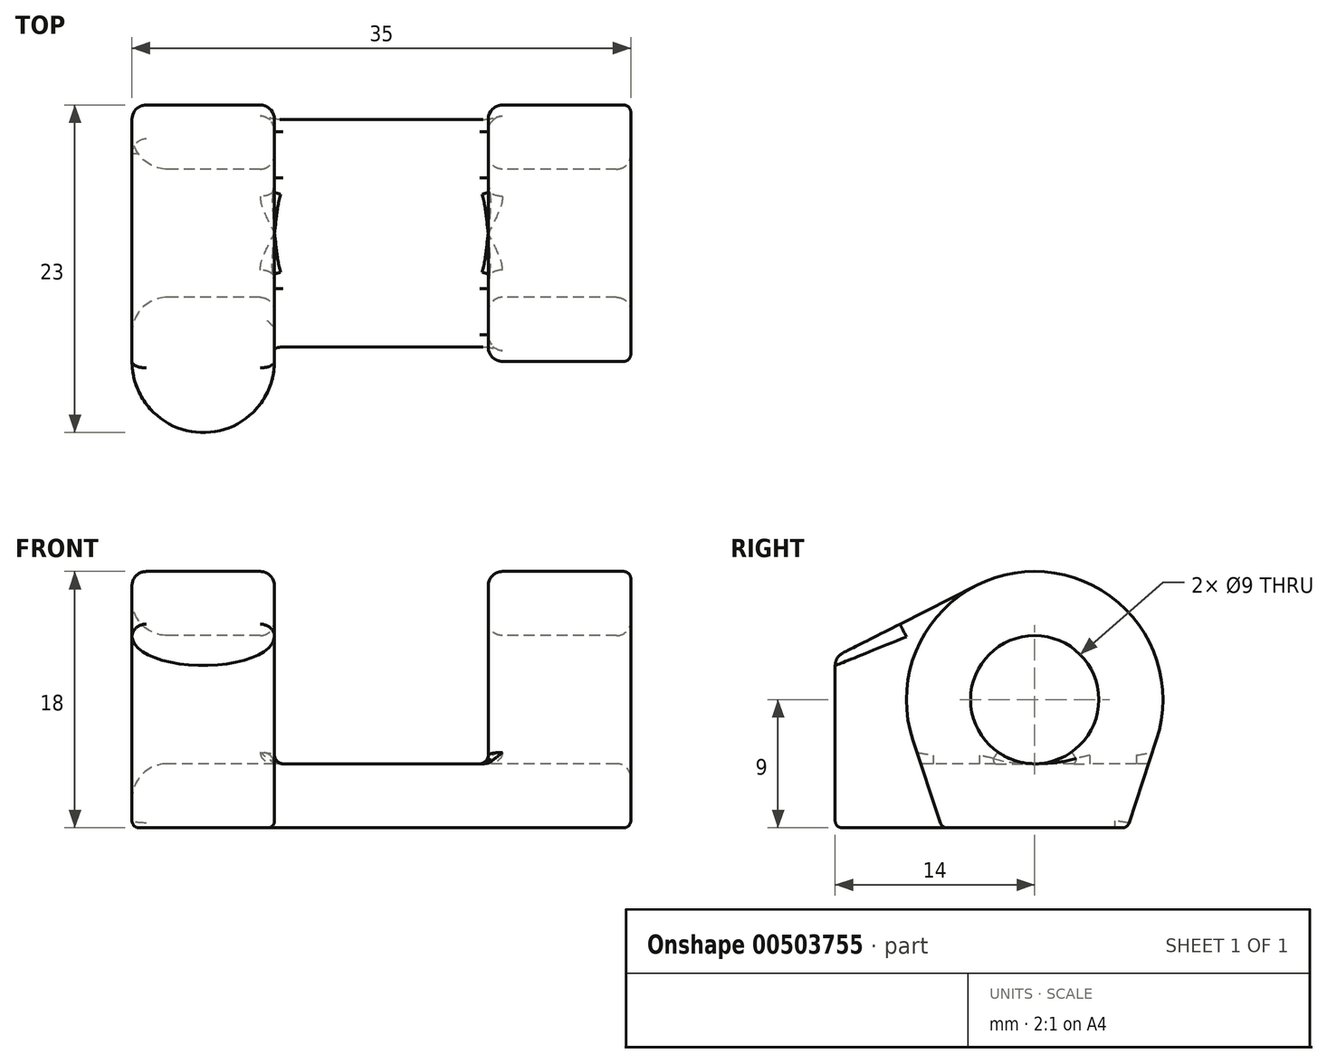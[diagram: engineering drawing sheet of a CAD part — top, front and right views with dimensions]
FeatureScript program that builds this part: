
annotation { "Feature Type Name" : "Feature", "Feature Type Description" : "" }
export const myFeature = defineFeature(function(context is Context, id is Id, definition is map)
    precondition{}
    {
        {
            var Q0;
            Q0=qCreatedBy(makeId("Right.planeOp"),FACE);
            var sketch = newSketch(context, id + "F0", { "sketchPlane" : qUnion([Q0])});
            skArc(sketch, "E0", {"start": v(8.54, -2.83) * mm, "mid": v(0, 9) * mm, "end": v(-8.54, -2.83) * mm});
            skCircle(sketch, "E1", {"center": v(0, 0) * mm, "radius": 4.5 * mm});
            skLineSegment(sketch, "E2", {"start": v(6.5, -9) * mm, "end": v(-6.5, -9) * mm});
            skLineSegment(sketch, "E3", {"start": v(8.54, -2.83) * mm, "end": v(6.5, -9) * mm});
            skLineSegment(sketch, "E4", {"start": v(-8.54, -2.83) * mm, "end": v(-6.5, -9) * mm});
            skSolve(sketch);
        }
        {
            var Q0;
            Q0=makeQuery(id+"F0.imprint","IMPRINT",FACE,{"disambiguationData":[TD([[makeQuery(id+"F0.imprint","IMPRINT",EDGE,{"derivedFrom":sQuery(id+"F0.wireOp",EDGE,"E0")}),1.0]])]});
            var Q1;
            Q1 = qSketchRegion(id + "F0", true);
            extrude(context, id + "F1", {"entities" : qUnion([Q0, Q1]), "depth" : 35 * mm});
        }
        {
            var Q0;
            Q0=qCreatedBy(makeId("Front.planeOp"),FACE);
            var sketch = newSketch(context, id + "F2", { "sketchPlane" : qUnion([Q0])});
            skLineSegment(sketch, "E5", {"start": v(10, 9) * mm, "end": v(25, 9) * mm});
            skLineSegment(sketch, "E6", {"start": v(25, -4.5) * mm, "end": v(10, -4.5) * mm});
            skLineSegment(sketch, "E7", {"start": v(10, -4.5) * mm, "end": v(10, 9) * mm});
            skLineSegment(sketch, "E8", {"start": v(25, -4.5) * mm, "end": v(25, 9) * mm});
            skSolve(sketch);
        }
        {
            var Q0;
            Q0 = qSketchRegion(id + "F2", true);
            extrude(context, id + "F3", {"entities" : qUnion([Q0]), "operationType" : NewBodyOperationType.REMOVE, "endBound" : BoundingType.SYMMETRIC, "oppositeDirection" : true, "depth" : 25 * mm});
        }
        {
            var Q0;
            Q0=makeQuery(id+"F1.opExtrude","CAP_FACE",FACE,{"disambiguationData":[OSD([sQuery(id+"F0.wireOp",EDGE,"E0"),sQuery(id+"F0.wireOp",EDGE,"E1")])],"isStart":true});
            var sketch = newSketch(context, id + "F4", { "sketchPlane" : qUnion([Q0])});
            skLineSegment(sketch, "E9", {"start": v(6.5, -9) * mm, "end": v(14, -9) * mm});
            skLineSegment(sketch, "E10", {"start": v(14, -9) * mm, "end": v(14, 3) * mm});
            skLineSegment(sketch, "E11", {"start": v(14, 3) * mm, "end": v(4.07, 8.03) * mm});
            skSolve(sketch);
        }
        {
            var Q0;
            Q0=makeQuery(id+"F4.imprint","IMPRINT",FACE,{"disambiguationData":[TD([[makeQuery(id+"F4.imprint","IMPRINT",EDGE,{"derivedFrom":sQuery(id+"F4.wireOp",EDGE,"E9")}),1.0]])]});
            var Q1;
            Q1=makeQuery(id+"F3.boolean.opBoolean","COPY",FACE,{"derivedFrom":makeQuery(id+"F3.opExtrude","SWEPT_FACE",FACE,{"disambiguationData":[OSD([sQuery(id+"F2.wireOp",EDGE,"E7")])]})});
            extrude(context, id + "F5", {"entities" : qUnion([Q0]), "operationType" : NewBodyOperationType.ADD, "endBound" : BoundingType.UP_TO_SURFACE, "oppositeDirection" : true, "endBoundEntityFace" : qUnion([Q1]), "depth" : 25 * mm});
        }
        {
            var Q0;
            Q0=qCreatedBy(makeId("Top.planeOp"),FACE);
            var sketch = newSketch(context, id + "F6", { "sketchPlane" : qUnion([Q0])});
            skArc(sketch, "E12", {"start": v(0, -9) * mm, "mid": v(5, -14) * mm, "end": v(10, -9) * mm});
            skLineSegment(sketch, "E13.0", {"start": v(10, -14) * mm, "end": v(0, -14) * mm});
            skLineSegment(sketch, "E14", {"start": v(0, -9) * mm, "end": v(0, -14) * mm});
            skLineSegment(sketch, "E15", {"start": v(10, -14) * mm, "end": v(10, -9) * mm});
            skSolve(sketch);
        }
        {
            var Q0;
            Q0 = qSketchRegion(id + "F6", true);
            extrude(context, id + "F7", {"entities" : qUnion([Q0]), "operationType" : NewBodyOperationType.REMOVE, "endBound" : BoundingType.SYMMETRIC, "oppositeDirection" : true, "depth" : 25 * mm});
        }
        {
            var Q0;
            Q0=makeQuery(id+"F3.boolean.opBoolean","INTERSECT",EDGE,{"disambiguationData":[OD(0.0)],"derivedFrom":[makeQuery(id+"F1.opExtrude","SWEPT_FACE",FACE,{"disambiguationData":[OSD([sQuery(id+"F0.wireOp",EDGE,"E0")])]}),makeQuery(id+"F3.opExtrude","SWEPT_FACE",FACE,{"disambiguationData":[OSD([sQuery(id+"F2.wireOp",EDGE,"E6")])]})]});
            var Q1;
            Q1=makeQuery(id+"F3.boolean.opBoolean","INTERSECT",EDGE,{"disambiguationData":[OD(1.0)],"derivedFrom":[makeQuery(id+"F1.opExtrude","SWEPT_FACE",FACE,{"disambiguationData":[OSD([sQuery(id+"F0.wireOp",EDGE,"E0")])]}),makeQuery(id+"F3.opExtrude","SWEPT_FACE",FACE,{"disambiguationData":[OSD([sQuery(id+"F2.wireOp",EDGE,"E6")])]})]});
            var Q2;
            Q2=makeQuery(id+"F1.opExtrude","SWEPT_EDGE",EDGE,{"disambiguationData":[OSD([sQuery(id+"F0.wireOp",EDGE,"E2"),sQuery(id+"F0.wireOp",EDGE,"E3")])]});
            var Q3;
            {var subQ0=sQuery(id+"F6.wireOp",EDGE,"E12");Q3=makeQuery(id+"F7.boolean.opBoolean","INTERSECT",EDGE,{"derivedFrom":[makeQuery(id+"F5.boolean.opBoolean","MERGE",FACE,{"derivedFrom":[makeQuery(id+"F1.opExtrude","SWEPT_FACE",FACE,{"disambiguationData":[OSD([sQuery(id+"F0.wireOp",EDGE,"E2")])]}),makeQuery(id+"F5.opExtrude","SWEPT_FACE",FACE,{"disambiguationData":[OSD([sQuery(id+"F4.wireOp",EDGE,"E9")])]})]}),makeQuery(id+"F7.opExtrude","SWEPT_FACE",FACE,{"disambiguationData":[OSD([subQ0]),TDD([makeQuery(id+"F6.imprint","IMPRINT",EDGE,{"disambiguationData":[TD([[makeQuery(id+"F6.imprint","INTERSECT",VERTEX,{"derivedFrom":[subQ0,sQuery(id+"F6.wireOp",EDGE,"E14")]}),-1.0]])],"derivedFrom":subQ0})])]}),makeQuery(id+"F7.opExtrude","SWEPT_FACE",FACE,{"disambiguationData":[OSD([subQ0]),TDD([makeQuery(id+"F6.imprint","IMPRINT",EDGE,{"disambiguationData":[TD([[makeQuery(id+"F6.imprint","INTERSECT",VERTEX,{"derivedFrom":[subQ0,sQuery(id+"F6.wireOp",EDGE,"E15")]}),1.0]])],"derivedFrom":subQ0})])]})]});}
            var Q4;
            Q4=makeQuery(id+"F1.opExtrude","SWEPT_EDGE",EDGE,{"disambiguationData":[OSD([sQuery(id+"F0.wireOp",EDGE,"E2"),sQuery(id+"F0.wireOp",EDGE,"E4")])]});
            var Q5;
            Q5=makeQuery(id+"F1.opExtrude","CAP_EDGE",EDGE,{"disambiguationData":[OSD([sQuery(id+"F0.wireOp",EDGE,"E4")])],"isStart":false});
            var Q6;
            Q6=makeQuery(id+"F1.opExtrude","CAP_EDGE",EDGE,{"disambiguationData":[OSD([sQuery(id+"F0.wireOp",EDGE,"E2")])],"isStart":false});
            fillet(context, id + "F8", {"entities" : qUnion([Q0, Q1, Q2, Q3, Q4, Q5, Q6]), "radius" : .5 * mm, "tangentPropagation" : true, "allowEdgeOverflow" : false});
        }
        {
            var Q0;
            Q0=makeQuery(id+"F1.opExtrude","CAP_EDGE",EDGE,{"disambiguationData":[OSD([sQuery(id+"F0.wireOp",EDGE,"E1")])],"isStart":true});
            fillet(context, id + "F9", {"entities" : qUnion([Q0]), "radius" : 2.5 * mm, "tangentPropagation" : true, "allowEdgeOverflow" : false});
        }
        {
            var Q0;
            Q0=makeQuery(id+"F1.opExtrude","CAP_EDGE",EDGE,{"disambiguationData":[OSD([sQuery(id+"F0.wireOp",EDGE,"E0")])],"isStart":true});
            var Q1;
            Q1=makeQuery(id+"F3.boolean.opBoolean","INTERSECT",EDGE,{"derivedFrom":[makeQuery(id+"F1.opExtrude","SWEPT_FACE",FACE,{"disambiguationData":[OSD([sQuery(id+"F0.wireOp",EDGE,"E1")])]}),makeQuery(id+"F3.opExtrude","SWEPT_FACE",FACE,{"disambiguationData":[OSD([sQuery(id+"F2.wireOp",EDGE,"E7")])]})]});
            var Q2;
            Q2=makeQuery(id+"F3.boolean.opBoolean","INTERSECT",EDGE,{"derivedFrom":[makeQuery(id+"F1.opExtrude","SWEPT_FACE",FACE,{"disambiguationData":[OSD([sQuery(id+"F0.wireOp",EDGE,"E1")])]}),makeQuery(id+"F3.opExtrude","SWEPT_FACE",FACE,{"disambiguationData":[OSD([sQuery(id+"F2.wireOp",EDGE,"E8")])]})]});
            var Q3;
            Q3=makeQuery(id+"F3.boolean.opBoolean","INTERSECT",EDGE,{"derivedFrom":[makeQuery(id+"F1.opExtrude","SWEPT_FACE",FACE,{"disambiguationData":[OSD([sQuery(id+"F0.wireOp",EDGE,"E0")])]}),makeQuery(id+"F3.opExtrude","SWEPT_FACE",FACE,{"disambiguationData":[OSD([sQuery(id+"F2.wireOp",EDGE,"E8")])]})]});
            var Q4;
            Q4=makeQuery(id+"F1.opExtrude","CAP_EDGE",EDGE,{"disambiguationData":[OSD([sQuery(id+"F0.wireOp",EDGE,"E0")])],"isStart":false});
            var Q5;
            Q5=makeQuery(id+"F1.opExtrude","CAP_EDGE",EDGE,{"disambiguationData":[OSD([sQuery(id+"F0.wireOp",EDGE,"E1")])],"isStart":false});
            fillet(context, id + "F10", {"entities" : qUnion([Q0, Q1, Q2, Q3, Q4, Q5]), "radius" : 1 * mm, "tangentPropagation" : true, "allowEdgeOverflow" : false});
        }
        {
            var Q0;
            Q0=makeQuery(id+"F3.boolean.opBoolean","COPY",EDGE,{"disambiguationData":[OD(0.0)],"derivedFrom":makeQuery(id+"F3.opExtrude","SWEPT_EDGE",EDGE,{"disambiguationData":[OSD([sQuery(id+"F2.wireOp",EDGE,"E6"),sQuery(id+"F2.wireOp",EDGE,"E8")])]})});
            var Q1;
            Q1=makeQuery(id+"F3.boolean.opBoolean","COPY",EDGE,{"disambiguationData":[OD(1.0)],"derivedFrom":makeQuery(id+"F3.opExtrude","SWEPT_EDGE",EDGE,{"disambiguationData":[OSD([sQuery(id+"F2.wireOp",EDGE,"E6"),sQuery(id+"F2.wireOp",EDGE,"E8")])]})});
            var Q2;
            {var subQ1=sQuery(id+"F2.wireOp",EDGE,"E6");var subQ3=sQuery(id+"F2.wireOp",EDGE,"E7");var subQ5=makeQuery(id+"F3.opExtrude","SWEPT_EDGE",EDGE,{"disambiguationData":[OSD([subQ1,subQ3])]});Q2=qUnion([makeQuery(id+"F3.boolean.opBoolean","COPY",EDGE,{"disambiguationData":[TD([makeQuery(id+"F1.opExtrude","SWEPT_FACE",FACE,{"disambiguationData":[OSD([sQuery(id+"F0.wireOp",EDGE,"E3")])]})])],"derivedFrom":subQ5}),makeQuery(id+"F3.boolean.opBoolean","COPY",EDGE,{"disambiguationData":[TD([makeQuery(id+"F1.opExtrude","SWEPT_FACE",FACE,{"disambiguationData":[OSD([sQuery(id+"F0.wireOp",EDGE,"E4")])]})])],"derivedFrom":subQ5})]);}
            var Q3;
            Q3=makeQuery(id+"F3.boolean.opBoolean","COPY",EDGE,{"disambiguationData":[OD(1.0)],"derivedFrom":makeQuery(id+"F3.opExtrude","SWEPT_EDGE",EDGE,{"disambiguationData":[OSD([sQuery(id+"F2.wireOp",EDGE,"E6"),sQuery(id+"F2.wireOp",EDGE,"E7")])]})});
            fillet(context, id + "F11", {"entities" : qUnion([Q0, Q1, Q2, Q3]), "radius" : .6 * mm, "tangentPropagation" : true, "allowEdgeOverflow" : false});
        }
    });
